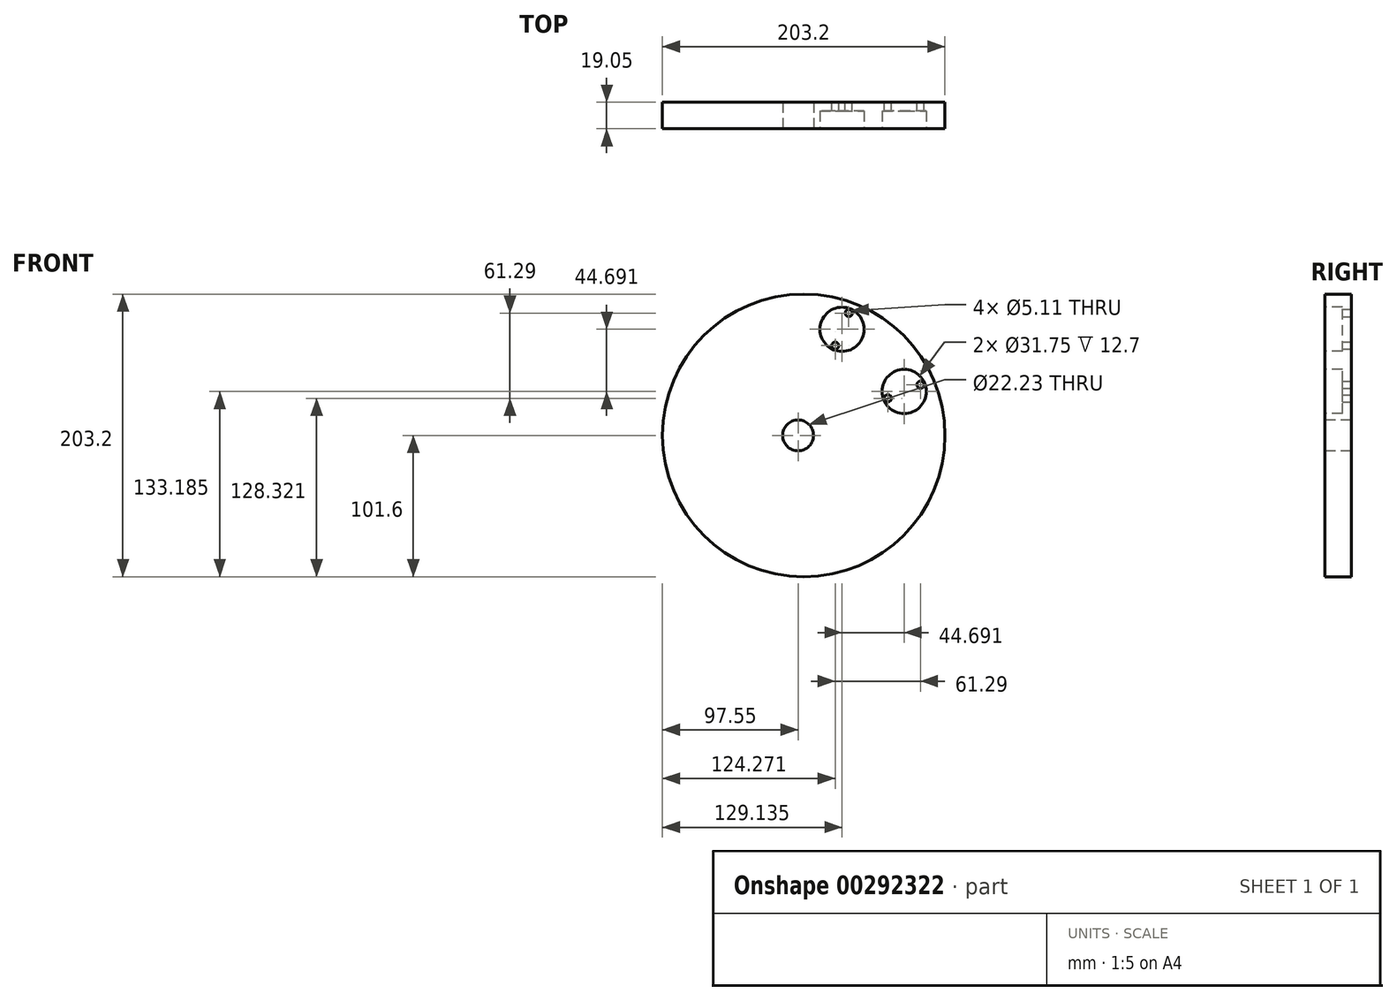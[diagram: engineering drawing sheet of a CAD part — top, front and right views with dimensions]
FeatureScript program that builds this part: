
annotation { "Feature Type Name" : "Feature", "Feature Type Description" : "" }
export const myFeature = defineFeature(function(context is Context, id is Id, definition is map)
    precondition{}
    {
        {
            var Q0;
            Q0=qCreatedBy(makeId("Front.planeOp"),FACE);
            var sketch = newSketch(context, id + "F0", { "sketchPlane" : qUnion([Q0])});
            skCircle(sketch, "E0", {"center": v(4.05, 0) * mm, "radius": 101.6 * mm});
            skSolve(sketch);
        }
        {
            var Q0;
            Q0=makeQuery(id+"F0.imprint","IMPRINT",FACE,{"disambiguationData":[TD([[makeQuery(id+"F0.imprint","IMPRINT",EDGE,{"derivedFrom":sQuery(id+"F0.wireOp",EDGE,"E0")}),1.0]])]});
            extrude(context, id + "F1", {"entities" : qUnion([Q0]), "depth" : 19.05 * mm});
        }
        {
            var Q0;
            Q0=makeQuery(id+"F1.opExtrude","CAP_FACE",FACE,{"disambiguationData":[OSD([sQuery(id+"F0.wireOp",EDGE,"E0")])],"isStart":false});
            var sketch = newSketch(context, id + "F2", { "sketchPlane" : qUnion([Q0])});
            skPoint(sketch, "E1", {"position": v(36.45, 88.01) * mm});
            skPoint(sketch, "E2", {"position": v(26.72, 64.54) * mm});
            skLineSegment(sketch, "E3", {"start": v(36.45, 88.01) * mm, "end": v(26.72, 64.54) * mm});
            skPoint(sketch, "E4", {"position": v(31.58, 76.28) * mm});
            skCircle(sketch, "E5", {"center": v(31.58, 76.28) * mm, "radius": 15.88 * mm});
            skPoint(sketch, "E6", {"position": v(88.01, 36.45) * mm});
            skPoint(sketch, "E7", {"position": v(64.54, 26.72) * mm});
            skLineSegment(sketch, "E8", {"start": v(88.01, 36.45) * mm, "end": v(64.54, 26.72) * mm});
            skPoint(sketch, "E9", {"position": v(76.28, 31.58) * mm});
            skCircle(sketch, "E10", {"center": v(76.28, 31.58) * mm, "radius": 15.88 * mm});
            skSolve(sketch);
        }
        {
            var Q0;
            Q0=makeQuery(id+"F2.imprint","IMPRINT",FACE,{"disambiguationData":[TD([[makeQuery(id+"F2.imprint","IMPRINT",EDGE,{"derivedFrom":sQuery(id+"F2.wireOp",EDGE,"E5")}),1.0]])]});
            var Q1;
            Q1=makeQuery(id+"F2.imprint","IMPRINT",FACE,{"disambiguationData":[TD([[makeQuery(id+"F2.imprint","IMPRINT",EDGE,{"derivedFrom":sQuery(id+"F2.wireOp",EDGE,"E10")}),1.0]])]});
            extrude(context, id + "F3", {"entities" : qUnion([Q0, Q1]), "operationType" : NewBodyOperationType.REMOVE, "oppositeDirection" : true, "depth" : 12.7 * mm});
        }
        {
            var Q0;
            Q0=makeQuery(id+"F1.opExtrude","CAP_FACE",FACE,{"disambiguationData":[OSD([sQuery(id+"F0.wireOp",EDGE,"E0")])],"isStart":false});
            var sketch = newSketch(context, id + "F4", { "sketchPlane" : qUnion([Q0])});
            skCircle(sketch, "E11", {"center": v(0, 0) * mm, "radius": 11.11 * mm});
            skSolve(sketch);
        }
        {
            var Q0;
            Q0 = qSketchRegion(id + "F4", true);
            extrude(context, id + "F5", {"entities" : qUnion([Q0]), "operationType" : NewBodyOperationType.REMOVE, "oppositeDirection" : true, "depth" : 19.05 * mm});
        }
        {
            var Q0;
            Q0=sQuery(id+"F2.wireOp",VERTEX,"E1");
            var Q1;
            Q1=sQuery(id+"F2.wireOp",VERTEX,"E2");
            var Q2;
            Q2=sQuery(id+"F2.wireOp",VERTEX,"E6");
            var Q3;
            Q3=sQuery(id+"F2.wireOp",VERTEX,"E7");
            var Q4;
            Q4=makeQuery(id+"F1.opExtrude","SWEPT_BODY",BODY,{"disambiguationData":[OSD([sQuery(id+"F0.wireOp",EDGE,"E0")])]});
            hole(context, id + "F6", {"style" : HoleStyle.SIMPLE, "endStyle" : HoleEndStyle.BLIND, "standardTappedOrClearance" : lookupTablePath({ "standard" : "ANSI", "fit" : "Normal (ASME)", "size" : "#10", "type" : "Clearance" }), "standardBlindInLast" : lookupTablePath({ "fit" : "Free", "standard" : "ANSI", "size" : "#10", "type" : "Clearance" }), "holeDiameter" : 5.1 * mm, "holeDepth" : 19.05 * mm, "isTappedThrough" : true, "tappedDepth" : 12.7 * mm, "tapClearance" : 3, "startFromSketch" : true, "locations" : qUnion([Q0, Q1, Q2, Q3]), "scope" : qUnion([Q4])});
        }
    });
